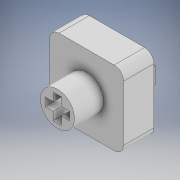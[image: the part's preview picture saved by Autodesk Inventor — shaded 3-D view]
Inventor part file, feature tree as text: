
AUTODESK INVENTOR PART (.ipt)
format: ipt  version: 2022 (Build 260153000, 153)  size: 231,936 bytes
history: native  units: in
note: dims shown in document units (in); Inventor stores cm internally (conversion verified against a paired STEP export)
features: sketch x4, extrude x3, plane x1, projected_geometry x1
ambient origin geometry x8: Origin, YZ Plane, XZ Plane, XY Plane, X Axis, Y Axis, Z Axis, Center Point
bodies: Body1 (feature_tree)
feature tree (9):
  sketch  "Sketch1"  dims[d3=0.2205in d4=0.1594in]
  plane  "Work Plane1"
  sketch  "Sketch2"  dims[d5=0.0531in d6=0.1594in]
  extrude  "Extrusion3"  Depth=0.1594in
  extrude  "Extrusion4"  Depth=0.1594in
  extrude  "Extrusion5"  Depth=0.5016in
  projected_geometry  "Projected Loop1"
  sketch  "Sketch3"  dims[d7=0.0531in d10=0.5016in]
  sketch  "Sketch4"  dims[d12=0.1969in d13=0.0in d14=0.2205in d15=0.1594in d16=0.0531in d17=0.1594in d18=0.0531in d19=0.189in d20=0.0in d21=0.0892in d22=0.2693in d23=0.0354in d24=0.0in]
